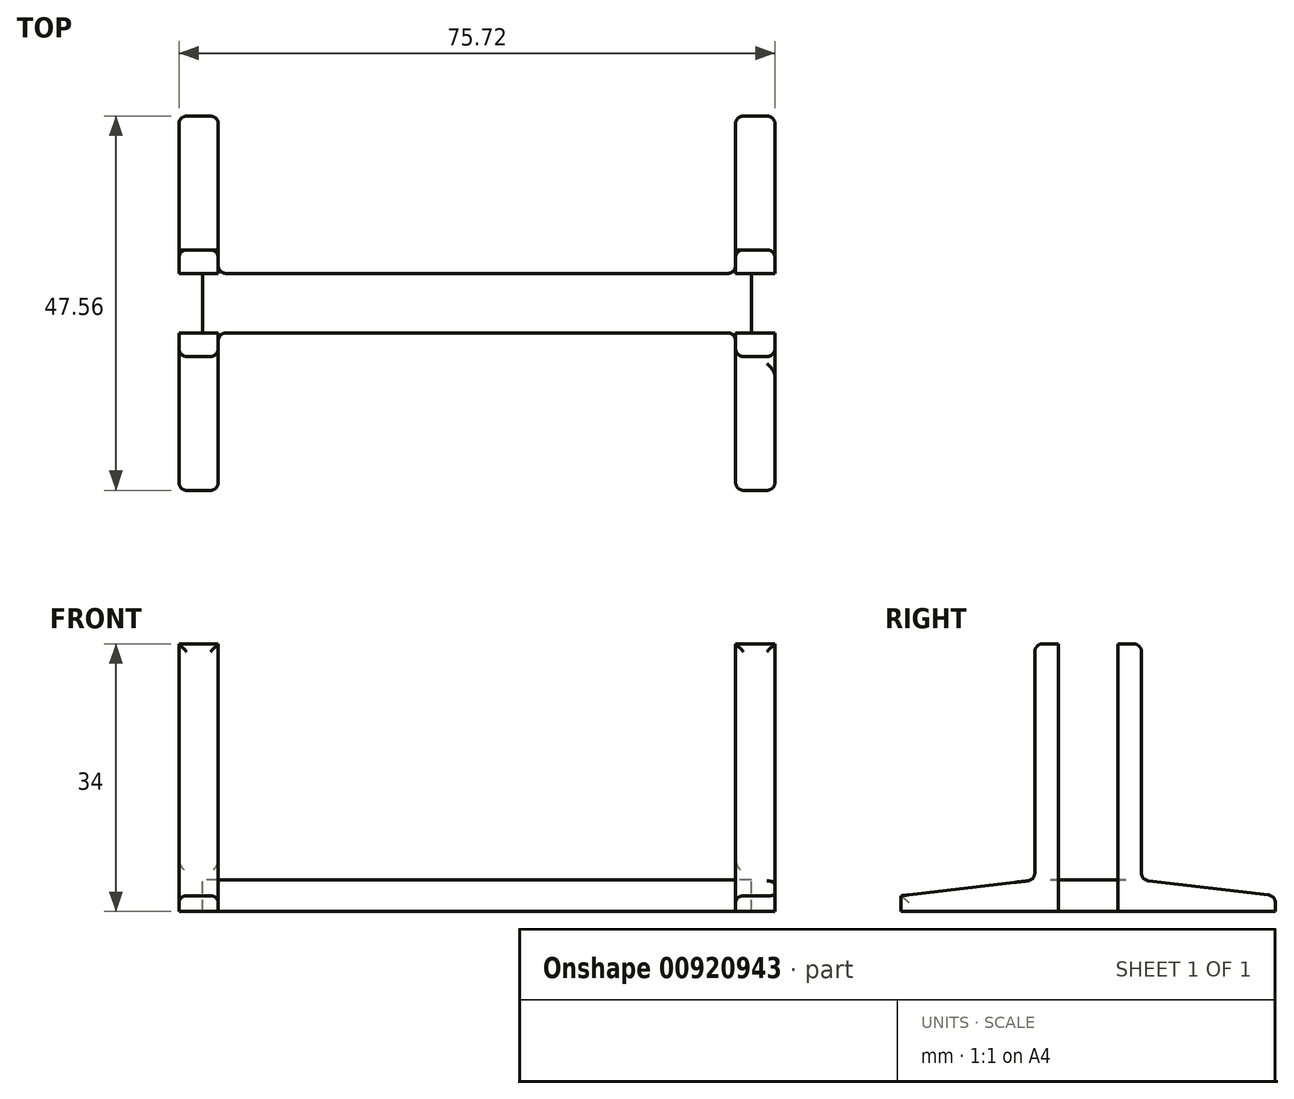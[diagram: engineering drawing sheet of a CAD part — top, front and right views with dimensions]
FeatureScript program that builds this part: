
annotation { "Feature Type Name" : "Feature", "Feature Type Description" : "" }
export const myFeature = defineFeature(function(context is Context, id is Id, definition is map)
    precondition{}
    {
        {
            var Q0;
            Q0=qCreatedBy(makeId("Top.planeOp"),FACE);
            var sketch = newSketch(context, id + "F0", { "sketchPlane" : qUnion([Q0])});
            skLineSegment(sketch, "E0.bottom", {"start": v(34.85, -3.78) * mm, "end": v(-34.86, -3.78) * mm});
            skLineSegment(sketch, "E0.top", {"start": v(34.86, 3.77) * mm, "end": v(-34.85, 3.77) * mm});
            skLineSegment(sketch, "E0.left", {"start": v(34.85, -3.78) * mm, "end": v(34.86, 3.77) * mm});
            skLineSegment(sketch, "E0.right", {"start": v(-34.86, -3.78) * mm, "end": v(-34.86, 3.77) * mm});
            skPoint(sketch, "E0.middle", {"position": v(0, 0) * mm});
            skLineSegment(sketch, "E1.bottom", {"start": v(-34.86, 3.77) * mm, "end": v(-37.86, 3.77) * mm});
            skLineSegment(sketch, "E1.top", {"start": v(-34.86, -3.78) * mm, "end": v(-37.86, -3.78) * mm});
            skLineSegment(sketch, "E1.left", {"start": v(-34.85, 3.77) * mm, "end": v(-34.86, -3.78) * mm});
            skLineSegment(sketch, "E1.right", {"start": v(-37.86, 3.77) * mm, "end": v(-37.86, -3.78) * mm});
            skLineSegment(sketch, "E2.bottom", {"start": v(34.86, 3.77) * mm, "end": v(37.85, 3.77) * mm});
            skLineSegment(sketch, "E2.top", {"start": v(34.85, -3.78) * mm, "end": v(37.85, -3.78) * mm});
            skLineSegment(sketch, "E2.left", {"start": v(34.86, 3.77) * mm, "end": v(34.85, -3.78) * mm});
            skLineSegment(sketch, "E2.right", {"start": v(37.85, 3.77) * mm, "end": v(37.85, -3.77) * mm});
            skLineSegment(sketch, "E3.bottom", {"start": v(-37.86, 3.77) * mm, "end": v(-32.86, 3.77) * mm});
            skLineSegment(sketch, "E3.top", {"start": v(-37.86, 6.77) * mm, "end": v(-32.86, 6.77) * mm});
            skLineSegment(sketch, "E3.left", {"start": v(-37.86, 3.77) * mm, "end": v(-37.86, 6.77) * mm});
            skLineSegment(sketch, "E3.right", {"start": v(-32.86, 3.77) * mm, "end": v(-32.86, 6.77) * mm});
            skLineSegment(sketch, "E4.bottom", {"start": v(-37.86, -3.78) * mm, "end": v(-32.86, -3.78) * mm});
            skLineSegment(sketch, "E4.top", {"start": v(-37.86, -6.78) * mm, "end": v(-32.86, -6.78) * mm});
            skLineSegment(sketch, "E4.left", {"start": v(-37.86, -3.78) * mm, "end": v(-37.86, -6.78) * mm});
            skLineSegment(sketch, "E4.right", {"start": v(-32.86, -3.78) * mm, "end": v(-32.86, -6.78) * mm});
            skLineSegment(sketch, "E5.bottom", {"start": v(37.85, -3.78) * mm, "end": v(32.85, -3.78) * mm});
            skLineSegment(sketch, "E5.top", {"start": v(37.85, -6.78) * mm, "end": v(32.85, -6.78) * mm});
            skLineSegment(sketch, "E5.left", {"start": v(37.85, -3.78) * mm, "end": v(37.85, -6.78) * mm});
            skLineSegment(sketch, "E5.right", {"start": v(32.85, -3.77) * mm, "end": v(32.85, -6.78) * mm});
            skLineSegment(sketch, "E6.bottom", {"start": v(37.85, 3.77) * mm, "end": v(32.85, 3.77) * mm});
            skLineSegment(sketch, "E6.top", {"start": v(37.85, 6.77) * mm, "end": v(32.85, 6.77) * mm});
            skLineSegment(sketch, "E6.left", {"start": v(37.85, 3.77) * mm, "end": v(37.85, 6.77) * mm});
            skLineSegment(sketch, "E6.right", {"start": v(32.85, 3.78) * mm, "end": v(32.85, 6.77) * mm});
            skLineSegment(sketch, "E7.top", {"start": v(-37.86, 23.77) * mm, "end": v(-32.86, 23.77) * mm});
            skLineSegment(sketch, "E7.left", {"start": v(-37.86, 3.77) * mm, "end": v(-37.86, 23.77) * mm});
            skLineSegment(sketch, "E7.right", {"start": v(-32.86, 3.77) * mm, "end": v(-32.86, 23.77) * mm});
            skLineSegment(sketch, "E8.top", {"start": v(-37.85, -23.78) * mm, "end": v(-32.86, -23.78) * mm});
            skLineSegment(sketch, "E8.left", {"start": v(-37.85, -3.78) * mm, "end": v(-37.85, -23.78) * mm});
            skLineSegment(sketch, "E8.right", {"start": v(-32.86, -3.78) * mm, "end": v(-32.86, -23.78) * mm});
            skLineSegment(sketch, "E9.top", {"start": v(37.85, 23.77) * mm, "end": v(32.85, 23.77) * mm});
            skLineSegment(sketch, "E9.left", {"start": v(37.85, 3.77) * mm, "end": v(37.85, 23.77) * mm});
            skLineSegment(sketch, "E9.right", {"start": v(32.85, 3.78) * mm, "end": v(32.85, 23.77) * mm});
            skLineSegment(sketch, "E10.top", {"start": v(37.86, -23.78) * mm, "end": v(32.85, -23.78) * mm});
            skLineSegment(sketch, "E10.left", {"start": v(37.85, -3.78) * mm, "end": v(37.85, -23.78) * mm});
            skLineSegment(sketch, "E10.right", {"start": v(32.85, -3.77) * mm, "end": v(32.85, -23.78) * mm});
            skSolve(sketch);
        }
        {
            var Q0;
            {var subQ0=sQuery(id+"F0.wireOp",EDGE,"E3.top");Q0=makeQuery(id+"F0.imprint","IMPRINT",FACE,{"disambiguationData":[TD([[makeQuery(id+"F0.imprint","IMPRINT",EDGE,{"derivedFrom":subQ0}),1.0]])]});}
            var Q1;
            {var subQ3=sQuery(id+"F0.wireOp",EDGE,"E3.top");Q1=makeQuery(id+"F0.imprint","IMPRINT",FACE,{"disambiguationData":[TD([[makeQuery(id+"F0.imprint","IMPRINT",EDGE,{"derivedFrom":subQ3}),-1.0]])]});}
            var Q2;
            {var subQ0=sQuery(id+"F0.wireOp",EDGE,"E4.top");Q2=makeQuery(id+"F0.imprint","IMPRINT",FACE,{"disambiguationData":[TD([[makeQuery(id+"F0.imprint","IMPRINT",EDGE,{"derivedFrom":subQ0}),-1.0]])]});}
            var Q3;
            {var subQ3=sQuery(id+"F0.wireOp",EDGE,"E5.top");Q3=makeQuery(id+"F0.imprint","IMPRINT",FACE,{"disambiguationData":[TD([[makeQuery(id+"F0.imprint","IMPRINT",EDGE,{"derivedFrom":subQ3}),-1.0]])]});}
            var Q4;
            {var subQ0=sQuery(id+"F0.wireOp",EDGE,"E6.top");Q4=makeQuery(id+"F0.imprint","IMPRINT",FACE,{"disambiguationData":[TD([[makeQuery(id+"F0.imprint","IMPRINT",EDGE,{"derivedFrom":subQ0}),-1.0]])]});}
            var Q5;
            {var subQ0=sQuery(id+"F0.wireOp",EDGE,"E1.left");Q5=makeQuery(id+"F0.imprint","IMPRINT",FACE,{"disambiguationData":[TD([[makeQuery(id+"F0.imprint","IMPRINT",EDGE,{"derivedFrom":subQ0}),-1.0]])]});}
            var Q6;
            {var subQ3=sQuery(id+"F0.wireOp",EDGE,"E4.top");Q6=makeQuery(id+"F0.imprint","IMPRINT",FACE,{"disambiguationData":[TD([[makeQuery(id+"F0.imprint","IMPRINT",EDGE,{"derivedFrom":subQ3}),1.0]])]});}
            var Q7;
            {var subQ3=sQuery(id+"F0.wireOp",EDGE,"E0.bottom");Q7=makeQuery(id+"F0.imprint","IMPRINT",FACE,{"disambiguationData":[TD([[makeQuery(id+"F0.imprint","IMPRINT",EDGE,{"derivedFrom":subQ3}),-1.0]])]});}
            var Q8;
            {var subQ0=sQuery(id+"F0.wireOp",EDGE,"E2.left");Q8=makeQuery(id+"F0.imprint","IMPRINT",FACE,{"disambiguationData":[TD([[makeQuery(id+"F0.imprint","IMPRINT",EDGE,{"derivedFrom":subQ0}),1.0]])]});}
            var Q9;
            {var subQ3=sQuery(id+"F0.wireOp",EDGE,"E6.top");Q9=makeQuery(id+"F0.imprint","IMPRINT",FACE,{"disambiguationData":[TD([[makeQuery(id+"F0.imprint","IMPRINT",EDGE,{"derivedFrom":subQ3}),1.0]])]});}
            var Q10;
            {var subQ0=sQuery(id+"F0.wireOp",EDGE,"E5.top");Q10=makeQuery(id+"F0.imprint","IMPRINT",FACE,{"disambiguationData":[TD([[makeQuery(id+"F0.imprint","IMPRINT",EDGE,{"derivedFrom":subQ0}),1.0]])]});}
            extrude(context, id + "F1", {"entities" : qUnion([Q0, Q1, Q2, Q3, Q4, Q5, Q6, Q7, Q8, Q9, Q10]), "oppositeDirection" : true, "depth" : 4 * mm, "offsetDistance" : 25 * mm});
        }
        {
            var Q0;
            {var subQ3=sQuery(id+"F0.wireOp",EDGE,"E3.top");Q0=makeQuery(id+"F0.imprint","IMPRINT",FACE,{"disambiguationData":[TD([[makeQuery(id+"F0.imprint","IMPRINT",EDGE,{"derivedFrom":subQ3}),-1.0]])]});}
            var Q1;
            {var subQ0=sQuery(id+"F0.wireOp",EDGE,"E1.left");Q1=makeQuery(id+"F0.imprint","IMPRINT",FACE,{"disambiguationData":[TD([[makeQuery(id+"F0.imprint","IMPRINT",EDGE,{"derivedFrom":subQ0}),-1.0]])]});}
            var Q2;
            {var subQ3=sQuery(id+"F0.wireOp",EDGE,"E4.top");Q2=makeQuery(id+"F0.imprint","IMPRINT",FACE,{"disambiguationData":[TD([[makeQuery(id+"F0.imprint","IMPRINT",EDGE,{"derivedFrom":subQ3}),1.0]])]});}
            var Q3;
            {var subQ3=sQuery(id+"F0.wireOp",EDGE,"E6.top");Q3=makeQuery(id+"F0.imprint","IMPRINT",FACE,{"disambiguationData":[TD([[makeQuery(id+"F0.imprint","IMPRINT",EDGE,{"derivedFrom":subQ3}),1.0]])]});}
            var Q4;
            {var subQ0=sQuery(id+"F0.wireOp",EDGE,"E2.left");Q4=makeQuery(id+"F0.imprint","IMPRINT",FACE,{"disambiguationData":[TD([[makeQuery(id+"F0.imprint","IMPRINT",EDGE,{"derivedFrom":subQ0}),1.0]])]});}
            var Q5;
            {var subQ3=sQuery(id+"F0.wireOp",EDGE,"E5.top");Q5=makeQuery(id+"F0.imprint","IMPRINT",FACE,{"disambiguationData":[TD([[makeQuery(id+"F0.imprint","IMPRINT",EDGE,{"derivedFrom":subQ3}),-1.0]])]});}
            extrude(context, id + "F2", {"entities" : qUnion([Q0, Q1, Q2, Q3, Q4, Q5]), "operationType" : NewBodyOperationType.ADD, "depth" : 30 * mm, "offsetDistance" : 25 * mm});
        }
        {
            var Q0;
            {var subQ0=sQuery(id+"F0.wireOp",EDGE,"E10.left");var subQ1=sQuery(id+"F0.wireOp",EDGE,"E9.left");var subQ2=sQuery(id+"F0.wireOp",EDGE,"E2.right");Q0=makeQuery(id+"F2.boolean.opBoolean","MERGE",FACE,{"derivedFrom":[makeQuery(id+"F1.opExtrude","SWEPT_FACE",FACE,{"disambiguationData":[OSD([subQ2,subQ1,subQ0])]}),makeQuery(id+"F2.opExtrude","SWEPT_FACE",FACE,{"disambiguationData":[OSD([subQ2,subQ1,subQ0])]})]});}
            var sketch = newSketch(context, id + "F3", { "sketchPlane" : qUnion([Q0])});
            skLineSegment(sketch, "E11", {"start": v(-6.78, 0) * mm, "end": v(-23.78, -2) * mm});
            skLineSegment(sketch, "E12.0", {"start": v(-6.78, 0) * mm, "end": v(-23.78, 0) * mm});
            skLineSegment(sketch, "E13", {"start": v(6.77, 0) * mm, "end": v(23.77, -2) * mm});
            skLineSegment(sketch, "E14", {"start": v(6.77, 0) * mm, "end": v(23.77, 0) * mm});
            skLineSegment(sketch, "E15", {"start": v(23.77, 0) * mm, "end": v(23.77, -2) * mm});
            skLineSegment(sketch, "E16", {"start": v(-23.78, 0) * mm, "end": v(-23.78, -2) * mm});
            skSolve(sketch);
        }
        {
            var Q0;
            Q0=makeQuery(id+"F3.imprint","IMPRINT",FACE,{"disambiguationData":[TD([[makeQuery(id+"F3.imprint","IMPRINT",EDGE,{"derivedFrom":sQuery(id+"F3.wireOp",EDGE,"E11")}),-1.0]])]});
            var Q1;
            Q1=makeQuery(id+"F3.imprint","IMPRINT",FACE,{"disambiguationData":[TD([[makeQuery(id+"F3.imprint","IMPRINT",EDGE,{"derivedFrom":sQuery(id+"F3.wireOp",EDGE,"E13")}),1.0]])]});
            extrude(context, id + "F4", {"entities" : qUnion([Q0, Q1]), "operationType" : NewBodyOperationType.REMOVE, "endBound" : BoundingType.THROUGH_ALL, "oppositeDirection" : true, "depth" : 25 * mm, "offsetDistance" : 25 * mm});
        }
        {
            var Q0;
            Q0=makeQuery(id+"F2.opExtrude","CAP_EDGE",EDGE,{"disambiguationData":[OSD([sQuery(id+"F0.wireOp",EDGE,"E1.right"),sQuery(id+"F0.wireOp",EDGE,"E7.left"),sQuery(id+"F0.wireOp",EDGE,"E8.left")])],"isStart":false});
            var Q1;
            Q1=makeQuery(id+"F2.opExtrude","CAP_EDGE",EDGE,{"disambiguationData":[OSD([sQuery(id+"F0.wireOp",EDGE,"E4.top")])],"isStart":false});
            var Q2;
            Q2=makeQuery(id+"F2.opExtrude","SWEPT_EDGE",EDGE,{"disambiguationData":[OSD([sQuery(id+"F0.wireOp",EDGE,"E4.top"),sQuery(id+"F0.wireOp",EDGE,"E8.left")])]});
            var Q3;
            Q3=makeQuery(id+"F2.opExtrude","CAP_EDGE",EDGE,{"disambiguationData":[OSD([sQuery(id+"F0.wireOp",EDGE,"E5.top")])],"isStart":false});
            var Q4;
            Q4=makeQuery(id+"F2.opExtrude","CAP_EDGE",EDGE,{"disambiguationData":[OSD([sQuery(id+"F0.wireOp",EDGE,"E2.right"),sQuery(id+"F0.wireOp",EDGE,"E9.left"),sQuery(id+"F0.wireOp",EDGE,"E10.left")])],"isStart":false});
            var Q5;
            Q5=makeQuery(id+"F2.opExtrude","SWEPT_EDGE",EDGE,{"disambiguationData":[OSD([sQuery(id+"F0.wireOp",EDGE,"E5.top"),sQuery(id+"F0.wireOp",EDGE,"E10.left")])]});
            var Q6;
            Q6=makeQuery(id+"F4.boolean.opBoolean","COPY",EDGE,{"derivedFrom":makeQuery(id+"F4.opExtrude","CAP_EDGE",EDGE,{"disambiguationData":[OSD([sQuery(id+"F3.wireOp",EDGE,"E11")])],"isStart":true})});
            var Q7;
            {var subQ0=sQuery(id+"F0.wireOp",EDGE,"E10.top");var subQ1=sQuery(id+"F3.wireOp",EDGE,"E11");Q7=makeQuery(id+"F4.boolean.opBoolean","COPY",EDGE,{"disambiguationData":[topologyDisambiguationEdgeConnected([makeQuery(id+"F1.opExtrude","SWEPT_FACE",FACE,{"disambiguationData":[OSD([subQ0])]})])],"derivedFrom":makeQuery(id+"F4.opExtrude","SWEPT_EDGE",EDGE,{"disambiguationData":[OSD([subQ0,sQuery(id+"F0.wireOp",EDGE,"E10.left"),subQ1,sQuery(id+"F3.wireOp",EDGE,"E16")])]})});}
            var Q8;
            Q8=makeQuery(id+"F1.opExtrude","SWEPT_EDGE",EDGE,{"disambiguationData":[OSD([sQuery(id+"F0.wireOp",EDGE,"E10.top"),sQuery(id+"F0.wireOp",EDGE,"E10.left")])]});
            var Q9;
            Q9=makeQuery(id+"F1.opExtrude","SWEPT_EDGE",EDGE,{"disambiguationData":[OSD([sQuery(id+"F0.wireOp",EDGE,"E10.top"),sQuery(id+"F0.wireOp",EDGE,"E10.right")])]});
            var Q10;
            {var subQ0=sQuery(id+"F0.wireOp",EDGE,"E10.right");Q10=makeQuery(id+"F4.boolean.opBoolean","INTERSECT",EDGE,{"derivedFrom":[makeQuery(id+"F2.boolean.opBoolean","MERGE",FACE,{"derivedFrom":[makeQuery(id+"F1.opExtrude","SWEPT_FACE",FACE,{"disambiguationData":[OSD([subQ0])]}),makeQuery(id+"F2.opExtrude","SWEPT_FACE",FACE,{"disambiguationData":[OSD([subQ0])]})]}),makeQuery(id+"F4.opExtrude","SWEPT_FACE",FACE,{"disambiguationData":[OSD([sQuery(id+"F3.wireOp",EDGE,"E11")])]})]});}
            var Q11;
            Q11=makeQuery(id+"F2.opExtrude","SWEPT_EDGE",EDGE,{"disambiguationData":[OSD([sQuery(id+"F0.wireOp",EDGE,"E5.top"),sQuery(id+"F0.wireOp",EDGE,"E10.right")])]});
            var Q12;
            {var subQ0=sQuery(id+"F3.wireOp",EDGE,"E11");Q12=makeQuery(id+"F4.boolean.opBoolean","COPY",EDGE,{"disambiguationData":[topologyDisambiguationEdgeConnected([makeQuery(id+"F1.opExtrude","SWEPT_FACE",FACE,{"disambiguationData":[OSD([sQuery(id+"F0.wireOp",EDGE,"E8.top")])]})])],"derivedFrom":makeQuery(id+"F4.opExtrude","SWEPT_EDGE",EDGE,{"disambiguationData":[OSD([sQuery(id+"F0.wireOp",EDGE,"E10.top"),sQuery(id+"F0.wireOp",EDGE,"E10.left"),subQ0,sQuery(id+"F3.wireOp",EDGE,"E16")])]})});}
            var Q13;
            Q13=makeQuery(id+"F1.opExtrude","SWEPT_EDGE",EDGE,{"disambiguationData":[OSD([sQuery(id+"F0.wireOp",EDGE,"E8.top"),sQuery(id+"F0.wireOp",EDGE,"E8.left")])]});
            var Q14;
            Q14=makeQuery(id+"F1.opExtrude","SWEPT_EDGE",EDGE,{"disambiguationData":[OSD([sQuery(id+"F0.wireOp",EDGE,"E8.top"),sQuery(id+"F0.wireOp",EDGE,"E8.right")])]});
            var Q15;
            {var subQ0=sQuery(id+"F0.wireOp",EDGE,"E8.left");var subQ1=sQuery(id+"F0.wireOp",EDGE,"E7.left");var subQ2=sQuery(id+"F0.wireOp",EDGE,"E1.right");Q15=makeQuery(id+"F4.boolean.opBoolean","INTERSECT",EDGE,{"derivedFrom":[makeQuery(id+"F2.boolean.opBoolean","MERGE",FACE,{"derivedFrom":[makeQuery(id+"F1.opExtrude","SWEPT_FACE",FACE,{"disambiguationData":[OSD([subQ2,subQ1,subQ0])]}),makeQuery(id+"F2.opExtrude","SWEPT_FACE",FACE,{"disambiguationData":[OSD([subQ2,subQ1,subQ0])]})]}),makeQuery(id+"F4.opExtrude","SWEPT_FACE",FACE,{"disambiguationData":[OSD([sQuery(id+"F3.wireOp",EDGE,"E11")])]})]});}
            var Q16;
            {var subQ0=sQuery(id+"F0.wireOp",EDGE,"E8.right");Q16=makeQuery(id+"F4.boolean.opBoolean","INTERSECT",EDGE,{"derivedFrom":[makeQuery(id+"F2.boolean.opBoolean","MERGE",FACE,{"derivedFrom":[makeQuery(id+"F1.opExtrude","SWEPT_FACE",FACE,{"disambiguationData":[OSD([subQ0])]}),makeQuery(id+"F2.opExtrude","SWEPT_FACE",FACE,{"disambiguationData":[OSD([subQ0])]})]}),makeQuery(id+"F4.opExtrude","SWEPT_FACE",FACE,{"disambiguationData":[OSD([sQuery(id+"F3.wireOp",EDGE,"E11")])]})]});}
            var Q17;
            Q17=makeQuery(id+"F2.opExtrude","SWEPT_EDGE",EDGE,{"disambiguationData":[OSD([sQuery(id+"F0.wireOp",EDGE,"E4.top"),sQuery(id+"F0.wireOp",EDGE,"E8.right")])]});
            var Q18;
            Q18=makeQuery(id+"F2.opExtrude","CAP_EDGE",EDGE,{"disambiguationData":[OSD([sQuery(id+"F0.wireOp",EDGE,"E8.right")])],"isStart":false});
            var Q19;
            Q19=makeQuery(id+"F2.opExtrude","CAP_EDGE",EDGE,{"disambiguationData":[OSD([sQuery(id+"F0.wireOp",EDGE,"E10.right")])],"isStart":false});
            var Q20;
            Q20=makeQuery(id+"F2.opExtrude","CAP_EDGE",EDGE,{"disambiguationData":[OSD([sQuery(id+"F0.wireOp",EDGE,"E6.top")])],"isStart":false});
            var Q21;
            Q21=makeQuery(id+"F2.opExtrude","SWEPT_EDGE",EDGE,{"disambiguationData":[OSD([sQuery(id+"F0.wireOp",EDGE,"E6.top"),sQuery(id+"F0.wireOp",EDGE,"E9.left")])]});
            var Q22;
            {var subQ0=sQuery(id+"F0.wireOp",EDGE,"E5.top");Q22=makeQuery(id+"F4.boolean.opBoolean","MERGE",EDGE,{"derivedFrom":[makeQuery(id+"F2.opExtrude","CAP_EDGE",EDGE,{"disambiguationData":[OSD([subQ0])],"isStart":true})],"fromTools":[makeQuery(id+"F4.opExtrude","SWEPT_EDGE",EDGE,{"disambiguationData":[OSD([subQ0,sQuery(id+"F0.wireOp",EDGE,"E10.left"),sQuery(id+"F3.wireOp",EDGE,"E11"),sQuery(id+"F3.wireOp",EDGE,"E12.0")])]})]});}
            var Q23;
            Q23=makeQuery(id+"F4.boolean.opBoolean","MERGE",EDGE,{"derivedFrom":[makeQuery(id+"F2.opExtrude","CAP_EDGE",EDGE,{"disambiguationData":[OSD([sQuery(id+"F0.wireOp",EDGE,"E4.top")])],"isStart":true})],"fromTools":[makeQuery(id+"F4.opExtrude","SWEPT_EDGE",EDGE,{"disambiguationData":[OSD([sQuery(id+"F0.wireOp",EDGE,"E5.top"),sQuery(id+"F0.wireOp",EDGE,"E10.left"),sQuery(id+"F3.wireOp",EDGE,"E11"),sQuery(id+"F3.wireOp",EDGE,"E12.0")])]})]});
            var Q24;
            {var subQ0=sQuery(id+"F0.wireOp",EDGE,"E6.top");Q24=makeQuery(id+"F4.boolean.opBoolean","MERGE",EDGE,{"derivedFrom":[makeQuery(id+"F2.opExtrude","CAP_EDGE",EDGE,{"disambiguationData":[OSD([subQ0])],"isStart":true})],"fromTools":[makeQuery(id+"F4.opExtrude","SWEPT_EDGE",EDGE,{"disambiguationData":[OSD([subQ0,sQuery(id+"F0.wireOp",EDGE,"E9.left"),sQuery(id+"F3.wireOp",EDGE,"E13"),sQuery(id+"F3.wireOp",EDGE,"E14")])]})]});}
            var Q25;
            Q25=makeQuery(id+"F4.boolean.opBoolean","COPY",FACE,{"disambiguationData":[TD([makeQuery(id+"F1.opExtrude","SWEPT_FACE",FACE,{"disambiguationData":[OSD([sQuery(id+"F0.wireOp",EDGE,"E9.top")])]})])],"derivedFrom":makeQuery(id+"F4.opExtrude","SWEPT_FACE",FACE,{"disambiguationData":[OSD([sQuery(id+"F3.wireOp",EDGE,"E13")])]})});
            var Q26;
            Q26=makeQuery(id+"F1.opExtrude","SWEPT_EDGE",EDGE,{"disambiguationData":[OSD([sQuery(id+"F0.wireOp",EDGE,"E9.top"),sQuery(id+"F0.wireOp",EDGE,"E9.left")])]});
            var Q27;
            Q27=makeQuery(id+"F1.opExtrude","SWEPT_EDGE",EDGE,{"disambiguationData":[OSD([sQuery(id+"F0.wireOp",EDGE,"E9.top"),sQuery(id+"F0.wireOp",EDGE,"E9.right")])]});
            var Q28;
            Q28=makeQuery(id+"F4.boolean.opBoolean","COPY",FACE,{"disambiguationData":[TD([makeQuery(id+"F1.opExtrude","SWEPT_FACE",FACE,{"disambiguationData":[OSD([sQuery(id+"F0.wireOp",EDGE,"E7.top")])]})])],"derivedFrom":makeQuery(id+"F4.opExtrude","SWEPT_FACE",FACE,{"disambiguationData":[OSD([sQuery(id+"F3.wireOp",EDGE,"E13")])]})});
            var Q29;
            Q29=makeQuery(id+"F2.opExtrude","CAP_EDGE",EDGE,{"disambiguationData":[OSD([sQuery(id+"F0.wireOp",EDGE,"E3.top")])],"isStart":false});
            var Q30;
            Q30=makeQuery(id+"F2.opExtrude","CAP_EDGE",EDGE,{"disambiguationData":[OSD([sQuery(id+"F0.wireOp",EDGE,"E7.right")])],"isStart":false});
            var Q31;
            Q31=makeQuery(id+"F1.opExtrude","SWEPT_EDGE",EDGE,{"disambiguationData":[OSD([sQuery(id+"F0.wireOp",EDGE,"E7.top"),sQuery(id+"F0.wireOp",EDGE,"E7.right")])]});
            var Q32;
            Q32=makeQuery(id+"F1.opExtrude","SWEPT_EDGE",EDGE,{"disambiguationData":[OSD([sQuery(id+"F0.wireOp",EDGE,"E7.top"),sQuery(id+"F0.wireOp",EDGE,"E7.left")])]});
            var Q33;
            Q33=makeQuery(id+"F1.opExtrude","SWEPT_EDGE",EDGE,{"disambiguationData":[OSD([sQuery(id+"F0.wireOp",EDGE,"E0.bottom"),sQuery(id+"F0.wireOp",EDGE,"E4.bottom"),sQuery(id+"F0.wireOp",EDGE,"E8.right")])]});
            var Q34;
            Q34=makeQuery(id+"F1.opExtrude","SWEPT_EDGE",EDGE,{"disambiguationData":[OSD([sQuery(id+"F0.wireOp",EDGE,"E0.bottom"),sQuery(id+"F0.wireOp",EDGE,"E5.bottom"),sQuery(id+"F0.wireOp",EDGE,"E10.right")])]});
            var Q35;
            Q35=makeQuery(id+"F1.opExtrude","SWEPT_EDGE",EDGE,{"disambiguationData":[OSD([sQuery(id+"F0.wireOp",EDGE,"E0.top"),sQuery(id+"F0.wireOp",EDGE,"E3.bottom"),sQuery(id+"F0.wireOp",EDGE,"E7.right")])]});
            var Q36;
            Q36=makeQuery(id+"F1.opExtrude","SWEPT_EDGE",EDGE,{"disambiguationData":[OSD([sQuery(id+"F0.wireOp",EDGE,"E0.top"),sQuery(id+"F0.wireOp",EDGE,"E6.bottom"),sQuery(id+"F0.wireOp",EDGE,"E9.right")])]});
            var Q37;
            Q37=makeQuery(id+"F2.opExtrude","CAP_EDGE",EDGE,{"disambiguationData":[OSD([sQuery(id+"F0.wireOp",EDGE,"E9.right")])],"isStart":false});
            fillet(context, id + "F5", {"entities" : qUnion([Q0, Q1, Q2, Q3, Q4, Q5, Q6, Q7, Q8, Q9, Q10, Q11, Q12, Q13, Q14, Q15, Q16, Q17, Q18, Q19, Q20, Q21, Q22, Q23, Q24, Q25, Q26, Q27, Q28, Q29, Q30, Q31, Q32, Q33, Q34, Q35, Q36, Q37]), "radius" : 1 * mm, "tangentPropagation" : true, "allowEdgeOverflow" : false});
        }
    });
